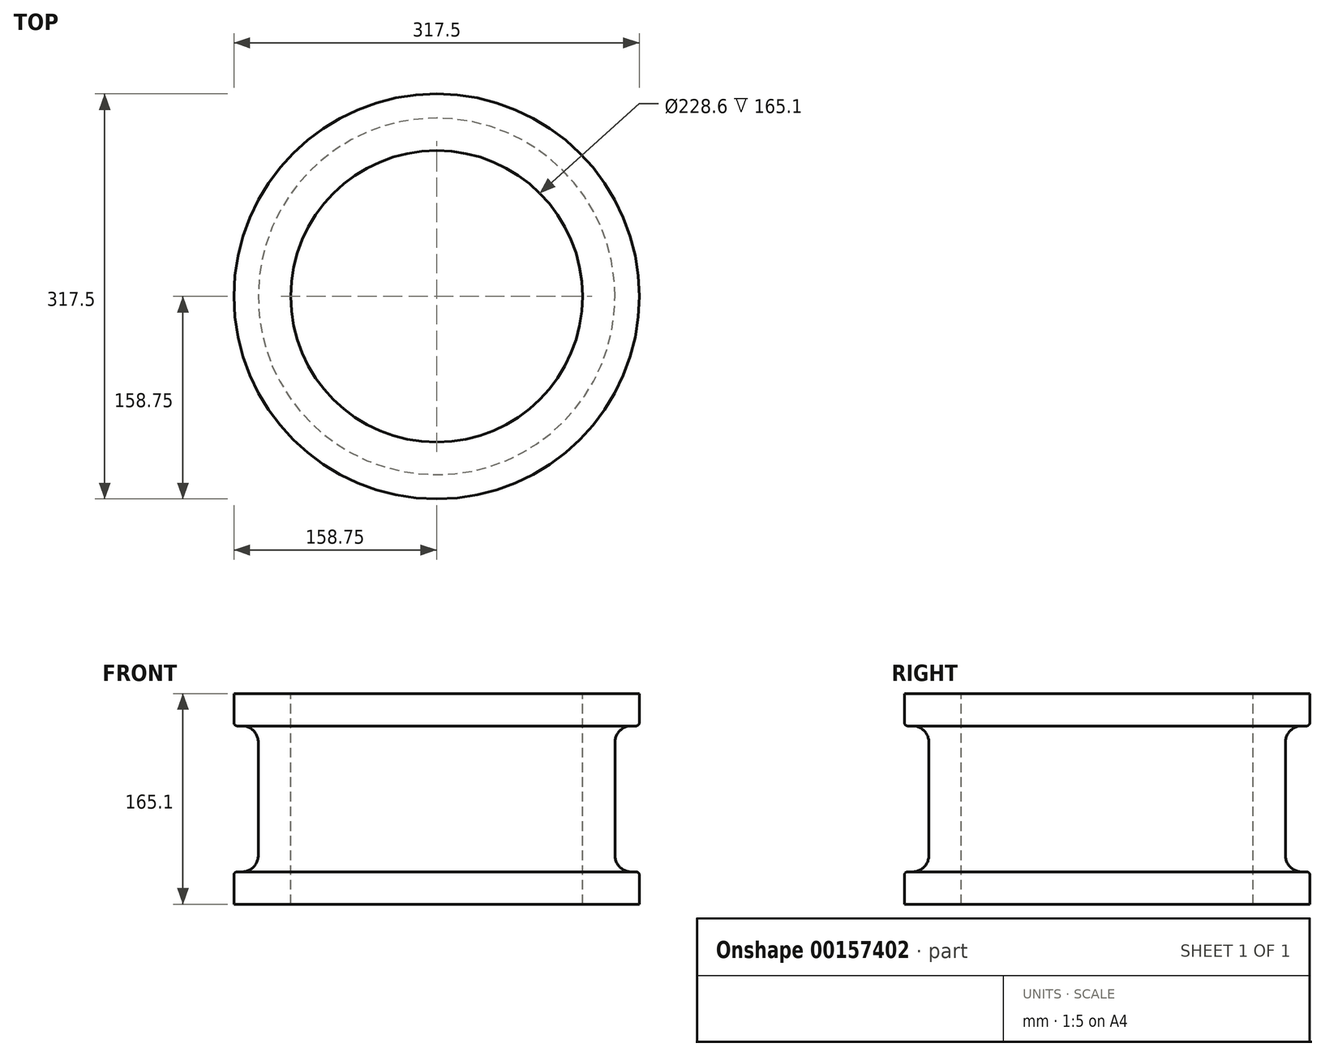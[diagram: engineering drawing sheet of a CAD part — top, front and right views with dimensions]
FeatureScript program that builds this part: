
annotation { "Feature Type Name" : "Feature", "Feature Type Description" : "" }
export const myFeature = defineFeature(function(context is Context, id is Id, definition is map)
    precondition{}
    {
        {
            var Q0;
            Q0=qCreatedBy(makeId("Front.planeOp"),FACE);
            var sketch = newSketch(context, id + "F0", { "sketchPlane" : qUnion([Q0])});
            skLineSegment(sketch, "E0", {"start": v(0, 0) * mm, "end": v(0, 165.1) * mm});
            skLineSegment(sketch, "E1", {"start": v(0, 165.1) * mm, "end": v(158.75, 165.1) * mm});
            skLineSegment(sketch, "E2", {"start": v(158.75, 165.1) * mm, "end": v(158.75, 139.7) * mm});
            skLineSegment(sketch, "E3", {"start": v(158.75, 139.7) * mm, "end": v(139.7, 139.7) * mm});
            skLineSegment(sketch, "E4", {"start": v(0, 0) * mm, "end": v(158.75, 0) * mm});
            skLineSegment(sketch, "E5", {"start": v(158.75, 0) * mm, "end": v(158.75, 25.4) * mm});
            skLineSegment(sketch, "E6", {"start": v(158.75, 25.4) * mm, "end": v(139.7, 25.4) * mm});
            skLineSegment(sketch, "E7", {"start": v(139.7, 25.4) * mm, "end": v(139.7, 139.7) * mm});
            skSolve(sketch);
        }
        {
            var Q0;
            Q0 = qSketchRegion(id + "F0", true);
            var Q1;
            Q1=sQuery(id+"F0.wireOp",EDGE,"E0");
            revolve(context, id + "F1", {"entities" : qUnion([Q0]), "axis" : qUnion([Q1]), "revolveType" : RevolveType.FULL});
        }
        {
            var Q0;
            Q0=makeQuery(id+"F1.opRevolve","SWEPT_EDGE",EDGE,{"disambiguationData":[OSD([sQuery(id+"F0.wireOp",EDGE,"E3"),sQuery(id+"F0.wireOp",EDGE,"E7")])]});
            var Q1;
            Q1=makeQuery(id+"F1.opRevolve","SWEPT_EDGE",EDGE,{"disambiguationData":[OSD([sQuery(id+"F0.wireOp",EDGE,"E6"),sQuery(id+"F0.wireOp",EDGE,"E7")])]});
            fillet(context, id + "F2", {"entities" : qUnion([Q0, Q1]), "radius" : 12.7 * mm, "tangentPropagation" : true, "allowEdgeOverflow" : false});
        }
        {
            var Q0;
            Q0=makeQuery(id+"F1.opRevolve","SWEPT_EDGE",EDGE,{"disambiguationData":[OSD([sQuery(id+"F0.wireOp",EDGE,"E5"),sQuery(id+"F0.wireOp",EDGE,"E6")])]});
            var Q1;
            Q1=makeQuery(id+"F1.opRevolve","SWEPT_EDGE",EDGE,{"disambiguationData":[OSD([sQuery(id+"F0.wireOp",EDGE,"E2"),sQuery(id+"F0.wireOp",EDGE,"E3")])]});
            fillet(context, id + "F3", {"entities" : qUnion([Q0, Q1]), "radius" : 2.54 * mm, "tangentPropagation" : true, "allowEdgeOverflow" : false});
        }
        {
            var Q0;
            Q0=makeQuery(id+"F1.opRevolve","SWEPT_FACE",FACE,{"disambiguationData":[OSD([sQuery(id+"F0.wireOp",EDGE,"E1")])]});
            var sketch = newSketch(context, id + "F4", { "sketchPlane" : qUnion([Q0])});
            skCircle(sketch, "E8", {"center": v(0, 0) * mm, "radius": 114.3 * mm});
            skSolve(sketch);
        }
        {
            var Q0;
            Q0 = qSketchRegion(id + "F4", true);
            extrude(context, id + "F5", {"entities" : qUnion([Q0]), "operationType" : NewBodyOperationType.REMOVE, "endBound" : BoundingType.THROUGH_ALL, "oppositeDirection" : true, "depth" : 25.4 * mm});
        }
    });
